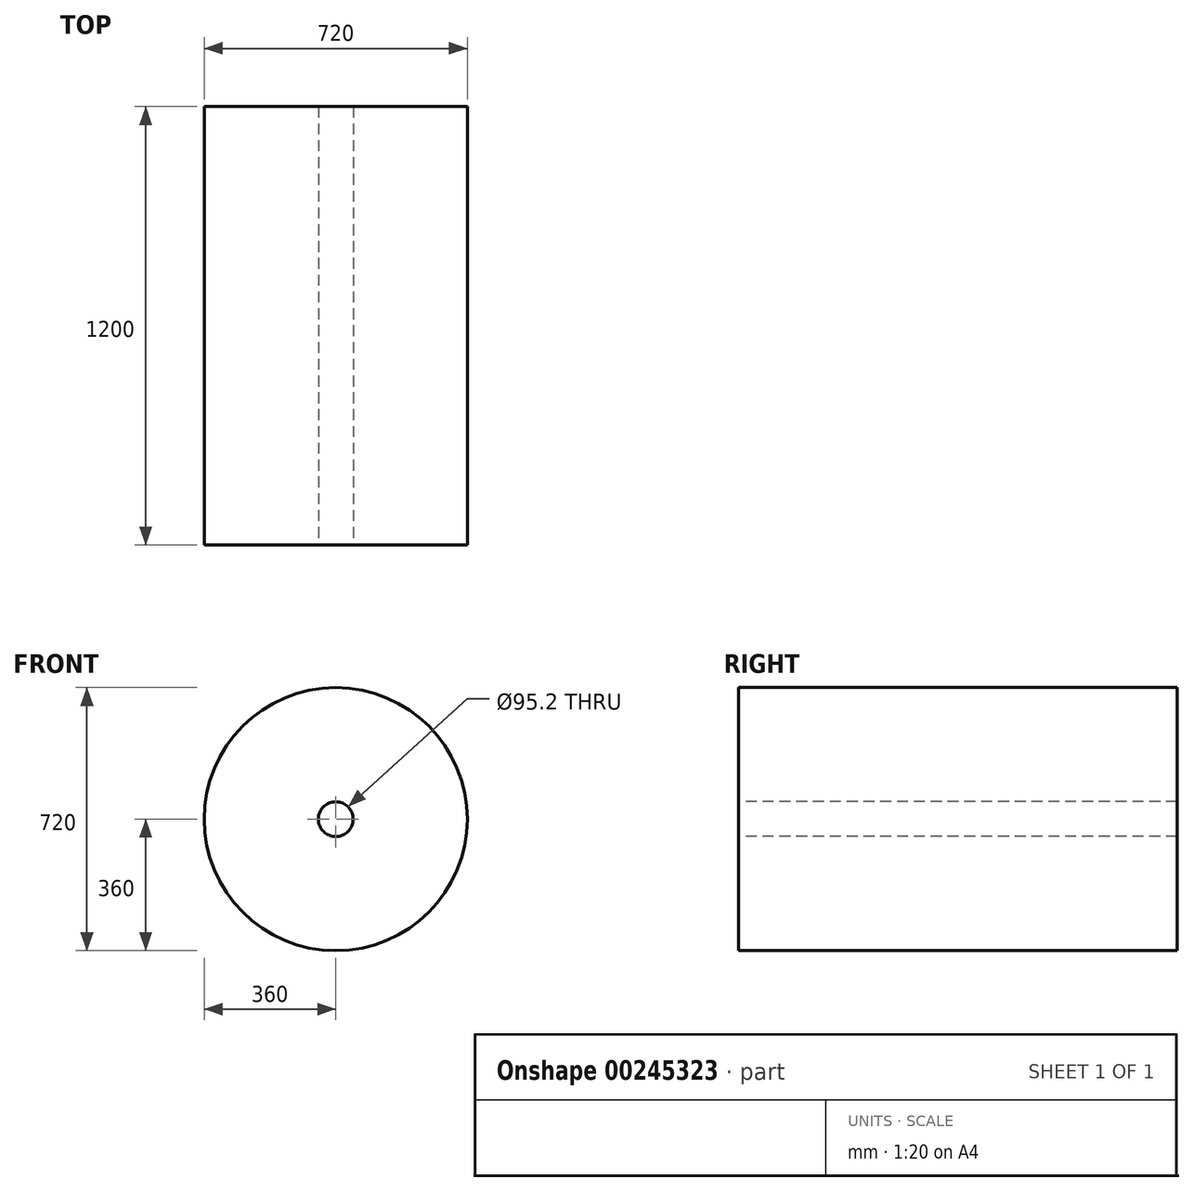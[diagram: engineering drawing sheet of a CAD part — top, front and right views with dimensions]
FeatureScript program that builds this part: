
annotation { "Feature Type Name" : "Feature", "Feature Type Description" : "" }
export const myFeature = defineFeature(function(context is Context, id is Id, definition is map)
    precondition{}
    {
        {
            var Q0;
            Q0=qCreatedBy(makeId("Front.planeOp"),FACE);
            var sketch = newSketch(context, id + "F0", { "sketchPlane" : qUnion([Q0])});
            skCircle(sketch, "E0", {"center": v(0, 0) * mm, "radius": 360 * mm});
            skCircle(sketch, "E1", {"center": v(0, 0) * mm, "radius": 47.6 * mm});
            skSolve(sketch);
        }
        {
            var Q0;
            Q0=makeQuery(id+"F0.imprint","IMPRINT",FACE,{"disambiguationData":[TD([[makeQuery(id+"F0.imprint","IMPRINT",EDGE,{"derivedFrom":sQuery(id+"F0.wireOp",EDGE,"E0")}),1.0]])]});
            extrude(context, id + "F1", {"entities" : qUnion([Q0]), "oppositeDirection" : true, "depth" : 1200 * mm, "offsetDistance" : 25 * mm});
        }
    });
